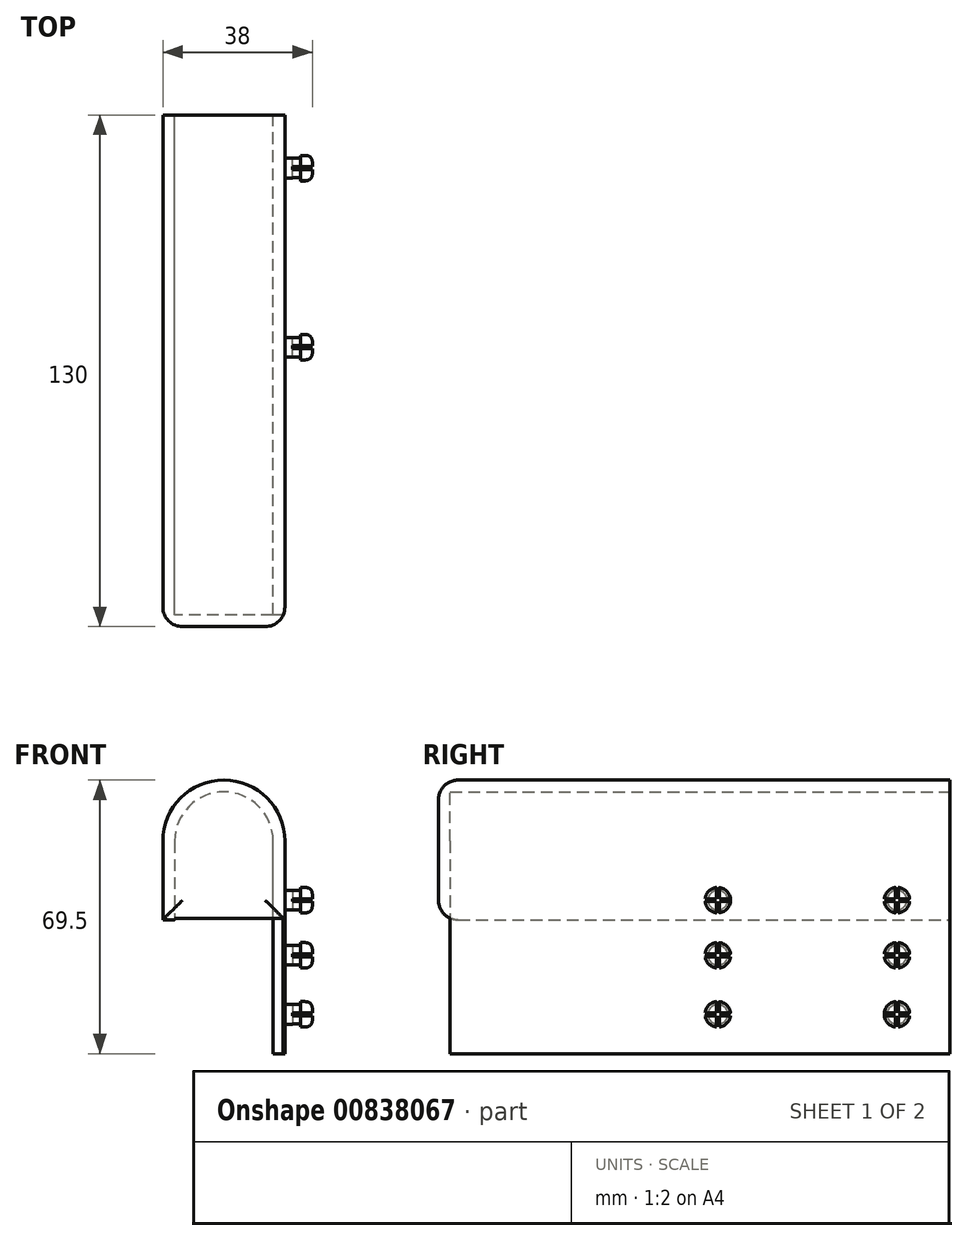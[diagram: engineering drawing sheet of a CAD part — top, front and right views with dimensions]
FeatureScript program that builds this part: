
annotation { "Feature Type Name" : "Feature", "Feature Type Description" : "" }
export const myFeature = defineFeature(function(context is Context, id is Id, definition is map)
    precondition{}
    {
        {
            var Q0;
            Q0=qCreatedBy(makeId("Front.planeOp"),FACE);
            cPlane(context, id + "F0", {"entities" : qUnion([Q0]), "cplaneType" : CPlaneType.OFFSET, "offset" : 31 * mm, "width" : 150 * mm, "height" : 150 * mm});
        }
        {
            var Q0;
            Q0=qCreatedBy(id+"F0.planeOp",FACE);
            var sketch = newSketch(context, id + "F1", { "sketchPlane" : qUnion([Q0])});
            skLineSegment(sketch, "E0.bottom", {"start": v(-95, 0) * mm, "end": v(-98, 0) * mm});
            skLineSegment(sketch, "E0.left", {"start": v(-95, 0) * mm, "end": v(-95, 54) * mm});
            skLineSegment(sketch, "E0.right", {"start": v(-98, 0) * mm, "end": v(-98, 54) * mm});
            skArc(sketch, "E1", {"start": v(-98, 54) * mm, "mid": v(-110.5, 66.5) * mm, "end": v(-123, 54) * mm});
            skArc(sketch, "E2", {"start": v(-95, 54) * mm, "mid": v(-110.5, 69.5) * mm, "end": v(-126, 54) * mm});
            skLineSegment(sketch, "E3.top", {"start": v(-126, 34) * mm, "end": v(-123, 34) * mm});
            skLineSegment(sketch, "E3.left", {"start": v(-126, 54) * mm, "end": v(-126, 34) * mm});
            skLineSegment(sketch, "E3.right", {"start": v(-123, 54) * mm, "end": v(-123, 34) * mm});
            skSolve(sketch);
        }
        {
            var Q0;
            Q0 = qSketchRegion(id + "F1", true);
            extrude(context, id + "F2", {"entities" : qUnion([Q0]), "depth" : (5 * 25.4) * mm, "offsetDistance" : 25 * mm});
        }
        {
            var Q0;
            Q0=makeQuery(id+"F2.opExtrude","CAP_FACE",FACE,{"disambiguationData":[OSD([sQuery(id+"F1.wireOp",EDGE,"E0.bottom"),sQuery(id+"F1.wireOp",EDGE,"E0.left"),sQuery(id+"F1.wireOp",EDGE,"E0.right"),sQuery(id+"F1.wireOp",EDGE,"E1"),sQuery(id+"F1.wireOp",EDGE,"E2"),sQuery(id+"F1.wireOp",EDGE,"E3.top"),sQuery(id+"F1.wireOp",EDGE,"E3.left"),sQuery(id+"F1.wireOp",EDGE,"E3.right")])],"isStart":false});
            var sketch = newSketch(context, id + "F3", { "sketchPlane" : qUnion([Q0])});
            skCircle(sketch, "E4", {"center": v(-110.5, 54) * mm, "radius": 15.5 * mm});
            skLineSegment(sketch, "E5.bottom", {"start": v(-126, 34) * mm, "end": v(-95, 34) * mm});
            skLineSegment(sketch, "E5.top", {"start": v(-126, 54) * mm, "end": v(-95, 54) * mm});
            skLineSegment(sketch, "E5.left", {"start": v(-126, 34) * mm, "end": v(-126, 54) * mm});
            skLineSegment(sketch, "E5.right", {"start": v(-95, 34) * mm, "end": v(-95, 54) * mm});
            skSolve(sketch);
        }
        {
            var Q0;
            Q0 = qSketchRegion(id + "F3", true);
            extrude(context, id + "F4", {"entities" : qUnion([Q0]), "operationType" : NewBodyOperationType.ADD, "depth" : 3 * mm, "offsetDistance" : 25 * mm});
        }
        {
            var Q0;
            Q0=makeQuery(id+"F4.opExtrude","CAP_EDGE",EDGE,{"disambiguationData":[OSD([sQuery(id+"F3.wireOp",EDGE,"E5.bottom")])],"isStart":false});
            fillet(context, id + "F5", {"entities" : qUnion([Q0]), "radius" : 5 * mm, "tangentPropagation" : true, "allowEdgeOverflow" : false});
        }
        {
            var Q0;
            Q0=makeQuery(id+"F4.opExtrude","CAP_EDGE",EDGE,{"disambiguationData":[OSD([sQuery(id+"F3.wireOp",EDGE,"E4")])],"isStart":false});
            fillet(context, id + "F6", {"entities" : qUnion([Q0]), "radius" : 5 * mm, "tangentPropagation" : true, "allowEdgeOverflow" : false});
        }
        {
            var Q0;
            Q0=makeQuery(id+"F4.boolean.opBoolean","MERGE",FACE,{"derivedFrom":[makeQuery(id+"F2.opExtrude","SWEPT_FACE",FACE,{"disambiguationData":[OSD([sQuery(id+"F1.wireOp",EDGE,"E0.left")])]}),makeQuery(id+"F4.opExtrude","SWEPT_FACE",FACE,{"disambiguationData":[OSD([sQuery(id+"F3.wireOp",EDGE,"E5.right")])]})]});
            var sketch = newSketch(context, id + "F7", { "sketchPlane" : qUnion([Q0])});
            skLineSegment(sketch, "E6", {"start": v(-44.5, -36.15) * mm, "end": v(-44.5, 70.7) * mm, "construction": true});
            skLineSegment(sketch, "E7", {"start": v(-5.8, 10) * mm, "end": v(3.25, 10) * mm, "construction": true});
            skLineSegment(sketch, "E8", {"start": v(-5.65, 25) * mm, "end": v(-3.87, 25) * mm, "construction": true});
            skLineSegment(sketch, "E9", {"start": v(-84.37, 39) * mm, "end": v(14.9, 39) * mm, "construction": true});
            skCircle(sketch, "E10", {"center": v(-44.5, 10) * mm, "radius": 2.5 * mm});
            skCircle(sketch, "E11", {"center": v(-44.5, 25) * mm, "radius": 2.5 * mm});
            skCircle(sketch, "E12", {"center": v(-44.5, 39) * mm, "radius": 2.5 * mm});
            skLineSegment(sketch, "E13", {"start": v(-90, -43.75) * mm, "end": v(-90, 131.84) * mm, "construction": true});
            skCircle(sketch, "E14", {"center": v(-90, 25) * mm, "radius": 2.5 * mm});
            skCircle(sketch, "E15", {"center": v(-90, 10) * mm, "radius": 2.5 * mm});
            skCircle(sketch, "E16", {"center": v(-90, 39) * mm, "radius": 2.5 * mm});
            skSolve(sketch);
        }
        {
            var Q0;
            Q0 = qSketchRegion(id + "F7", true);
            extrude(context, id + "F8", {"entities" : qUnion([Q0]), "operationType" : NewBodyOperationType.ADD, "depth" : 4 * mm, "offsetDistance" : 25 * mm});
        }
        {
            var Q0;
            Q0=makeQuery(id+"F8.opExtrude","CAP_FACE",FACE,{"disambiguationData":[OSD([sQuery(id+"F7.wireOp",EDGE,"E12")])],"isStart":false});
            var sketch = newSketch(context, id + "F9", { "sketchPlane" : qUnion([Q0])});
            skCircle(sketch, "E17", {"center": v(-44.5, 39) * mm, "radius": 3.25 * mm});
            skCircle(sketch, "E18", {"center": v(-44.5, 10) * mm, "radius": 3.25 * mm});
            skCircle(sketch, "E19", {"center": v(-44.5, 25) * mm, "radius": 3.25 * mm});
            skCircle(sketch, "E20", {"center": v(-90, 39) * mm, "radius": 3.25 * mm});
            skCircle(sketch, "E21", {"center": v(-90, 10) * mm, "radius": 3.25 * mm});
            skCircle(sketch, "E22", {"center": v(-90, 25) * mm, "radius": 3.25 * mm});
            skSolve(sketch);
        }
        {
            var Q0;
            Q0 = qSketchRegion(id + "F9", true);
            extrude(context, id + "F10", {"entities" : qUnion([Q0]), "operationType" : NewBodyOperationType.ADD, "depth" : 3 * mm, "offsetDistance" : 25 * mm});
        }
        {
            var Q0;
            Q0=makeQuery(id+"F10.opExtrude","CAP_EDGE",EDGE,{"disambiguationData":[OSD([sQuery(id+"F9.wireOp",EDGE,"E18")])],"isStart":false});
            var Q1;
            Q1=makeQuery(id+"F10.opExtrude","CAP_EDGE",EDGE,{"disambiguationData":[OSD([sQuery(id+"F9.wireOp",EDGE,"E19")])],"isStart":false});
            var Q2;
            Q2=makeQuery(id+"F10.opExtrude","CAP_EDGE",EDGE,{"disambiguationData":[OSD([sQuery(id+"F9.wireOp",EDGE,"E17")])],"isStart":false});
            var Q3;
            Q3=makeQuery(id+"F10.opExtrude","CAP_EDGE",EDGE,{"disambiguationData":[OSD([sQuery(id+"F9.wireOp",EDGE,"E20")])],"isStart":false});
            var Q4;
            Q4=makeQuery(id+"F10.opExtrude","CAP_EDGE",EDGE,{"disambiguationData":[OSD([sQuery(id+"F9.wireOp",EDGE,"E22")])],"isStart":false});
            var Q5;
            Q5=makeQuery(id+"F10.opExtrude","CAP_EDGE",EDGE,{"disambiguationData":[OSD([sQuery(id+"F9.wireOp",EDGE,"E21")])],"isStart":false});
            fillet(context, id + "F11", {"entities" : qUnion([Q0, Q1, Q2, Q3, Q4, Q5]), "radius" : 2 * mm, "rho" : 0.5, "crossSection" : FilletCrossSection.CONIC, "allowEdgeOverflow" : false});
        }
        {
            var Q0;
            Q0=makeQuery(id+"F10.opExtrude","CAP_FACE",FACE,{"disambiguationData":[OSD([sQuery(id+"F9.wireOp",EDGE,"E17")])],"isStart":false});
            var sketch = newSketch(context, id + "F12", { "sketchPlane" : qUnion([Q0])});
            skLineSegment(sketch, "E23.bottom", {"start": v(-47.75, 39.38) * mm, "end": v(-41.25, 39.38) * mm});
            skLineSegment(sketch, "E23.top", {"start": v(-47.75, 38.62) * mm, "end": v(-41.25, 38.62) * mm});
            skLineSegment(sketch, "E23.left", {"start": v(-47.75, 39.38) * mm, "end": v(-47.75, 38.62) * mm});
            skLineSegment(sketch, "E23.right", {"start": v(-41.25, 39.38) * mm, "end": v(-41.25, 38.62) * mm});
            skLineSegment(sketch, "E24.bottom", {"start": v(-47.75, 25.38) * mm, "end": v(-41.25, 25.38) * mm});
            skLineSegment(sketch, "E24.top", {"start": v(-47.75, 24.62) * mm, "end": v(-41.25, 24.62) * mm});
            skLineSegment(sketch, "E24.left", {"start": v(-47.75, 25.38) * mm, "end": v(-47.75, 24.62) * mm});
            skLineSegment(sketch, "E24.right", {"start": v(-41.25, 25.38) * mm, "end": v(-41.25, 24.62) * mm});
            skLineSegment(sketch, "E25.bottom", {"start": v(-47.6, 10.38) * mm, "end": v(-41.25, 10.38) * mm});
            skLineSegment(sketch, "E25.top", {"start": v(-47.6, 9.62) * mm, "end": v(-41.25, 9.62) * mm});
            skLineSegment(sketch, "E25.left", {"start": v(-47.6, 10.38) * mm, "end": v(-47.6, 9.62) * mm});
            skLineSegment(sketch, "E25.right", {"start": v(-41.25, 10.38) * mm, "end": v(-41.25, 9.62) * mm});
            skLineSegment(sketch, "E26.bottom", {"start": v(-44.88, 13.25) * mm, "end": v(-44.12, 13.25) * mm});
            skLineSegment(sketch, "E26.top", {"start": v(-44.88, 6.75) * mm, "end": v(-44.12, 6.75) * mm});
            skLineSegment(sketch, "E26.left", {"start": v(-44.88, 13.25) * mm, "end": v(-44.88, 6.75) * mm});
            skLineSegment(sketch, "E26.right", {"start": v(-44.12, 13.25) * mm, "end": v(-44.12, 6.75) * mm});
            skLineSegment(sketch, "E27.bottom", {"start": v(-44.88, 28.25) * mm, "end": v(-44.12, 28.25) * mm});
            skLineSegment(sketch, "E27.top", {"start": v(-44.88, 21.75) * mm, "end": v(-44.12, 21.75) * mm});
            skLineSegment(sketch, "E27.left", {"start": v(-44.88, 28.25) * mm, "end": v(-44.88, 21.75) * mm});
            skLineSegment(sketch, "E27.right", {"start": v(-44.12, 28.25) * mm, "end": v(-44.12, 21.75) * mm});
            skLineSegment(sketch, "E28.bottom", {"start": v(-44.88, 42.25) * mm, "end": v(-44.12, 42.25) * mm});
            skLineSegment(sketch, "E28.top", {"start": v(-44.88, 35.75) * mm, "end": v(-44.12, 35.75) * mm});
            skLineSegment(sketch, "E28.left", {"start": v(-44.88, 42.25) * mm, "end": v(-44.88, 35.75) * mm});
            skLineSegment(sketch, "E28.right", {"start": v(-44.12, 42.25) * mm, "end": v(-44.12, 35.75) * mm});
            skLineSegment(sketch, "E29.bottom", {"start": v(-93.25, 10.38) * mm, "end": v(-86.75, 10.38) * mm});
            skLineSegment(sketch, "E29.top", {"start": v(-93.25, 9.63) * mm, "end": v(-86.75, 9.63) * mm});
            skLineSegment(sketch, "E29.left", {"start": v(-93.25, 10.38) * mm, "end": v(-93.25, 9.63) * mm});
            skLineSegment(sketch, "E29.right", {"start": v(-86.75, 10.38) * mm, "end": v(-86.75, 9.63) * mm});
            skLineSegment(sketch, "E30.bottom", {"start": v(-93.25, 25.37) * mm, "end": v(-86.75, 25.37) * mm});
            skLineSegment(sketch, "E30.top", {"start": v(-93.25, 24.62) * mm, "end": v(-86.75, 24.62) * mm});
            skLineSegment(sketch, "E30.left", {"start": v(-93.25, 25.37) * mm, "end": v(-93.25, 24.62) * mm});
            skLineSegment(sketch, "E30.right", {"start": v(-86.75, 25.37) * mm, "end": v(-86.75, 24.62) * mm});
            skLineSegment(sketch, "E31.bottom", {"start": v(-93.25, 39.38) * mm, "end": v(-86.9, 39.38) * mm});
            skLineSegment(sketch, "E31.top", {"start": v(-93.25, 38.62) * mm, "end": v(-86.9, 38.62) * mm});
            skLineSegment(sketch, "E31.left", {"start": v(-93.25, 39.37) * mm, "end": v(-93.25, 38.62) * mm});
            skLineSegment(sketch, "E31.right", {"start": v(-86.9, 39.37) * mm, "end": v(-86.9, 38.62) * mm});
            skLineSegment(sketch, "E32.bottom", {"start": v(-90.38, 42.25) * mm, "end": v(-89.62, 42.25) * mm});
            skLineSegment(sketch, "E32.top", {"start": v(-90.38, 35.75) * mm, "end": v(-89.62, 35.75) * mm});
            skLineSegment(sketch, "E32.left", {"start": v(-90.38, 42.25) * mm, "end": v(-90.38, 35.75) * mm});
            skLineSegment(sketch, "E32.right", {"start": v(-89.62, 42.25) * mm, "end": v(-89.62, 35.75) * mm});
            skLineSegment(sketch, "E33.bottom", {"start": v(-90.38, 28.25) * mm, "end": v(-89.62, 28.25) * mm});
            skLineSegment(sketch, "E33.top", {"start": v(-90.38, 21.75) * mm, "end": v(-89.62, 21.75) * mm});
            skLineSegment(sketch, "E33.left", {"start": v(-90.38, 28.25) * mm, "end": v(-90.38, 21.75) * mm});
            skLineSegment(sketch, "E33.right", {"start": v(-89.62, 28.25) * mm, "end": v(-89.62, 21.75) * mm});
            skLineSegment(sketch, "E34.bottom", {"start": v(-90.38, 13.25) * mm, "end": v(-89.62, 13.25) * mm});
            skLineSegment(sketch, "E34.top", {"start": v(-90.38, 6.75) * mm, "end": v(-89.62, 6.75) * mm});
            skLineSegment(sketch, "E34.left", {"start": v(-90.38, 13.25) * mm, "end": v(-90.38, 6.75) * mm});
            skLineSegment(sketch, "E34.right", {"start": v(-89.62, 13.25) * mm, "end": v(-89.62, 6.75) * mm});
            skSolve(sketch);
        }
        {
            var Q0;
            Q0 = qSketchRegion(id + "F12", true);
            extrude(context, id + "F13", {"entities" : qUnion([Q0]), "operationType" : NewBodyOperationType.REMOVE, "oppositeDirection" : true, "depth" : 5 * mm, "offsetDistance" : 25 * mm});
        }
    });
